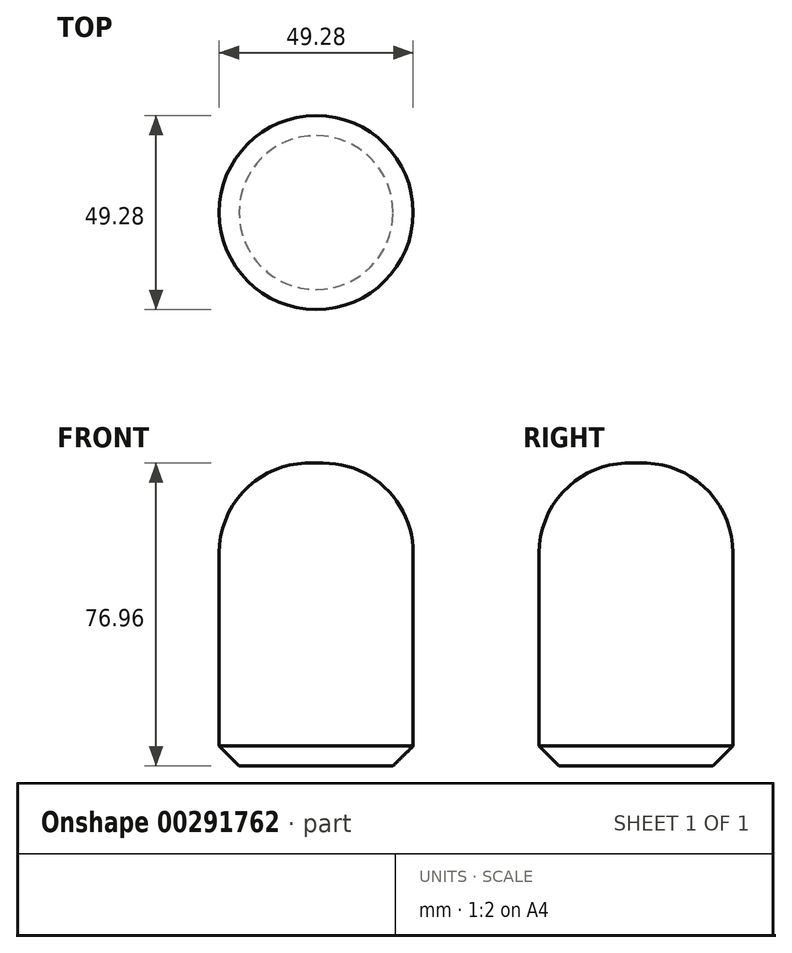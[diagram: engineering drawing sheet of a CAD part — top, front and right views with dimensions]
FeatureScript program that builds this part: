
annotation { "Feature Type Name" : "Feature", "Feature Type Description" : "" }
export const myFeature = defineFeature(function(context is Context, id is Id, definition is map)
    precondition{}
    {
        {
            var Q0;
            Q0=qCreatedBy(makeId("Top.planeOp"),FACE);
            var sketch = newSketch(context, id + "F0", { "sketchPlane" : qUnion([Q0])});
            skCircle(sketch, "E0", {"center": v(0, 0) * mm, "radius": 24.64 * mm});
            skSolve(sketch);
        }
        {
            var Q0;
            Q0=makeQuery(id+"F0.imprint","IMPRINT",FACE,{"disambiguationData":[TD([[makeQuery(id+"F0.imprint","IMPRINT",EDGE,{"derivedFrom":sQuery(id+"F0.wireOp",EDGE,"E0")}),1.0]])]});
            extrude(context, id + "F1", {"entities" : qUnion([Q0]), "depth" : 51.56 * mm});
        }
        {
            var Q0;
            Q0=makeQuery(id+"F1.opExtrude","CAP_EDGE",EDGE,{"disambiguationData":[OSD([sQuery(id+"F0.wireOp",EDGE,"E0")])],"isStart":true});
            chamfer(context, id + "F2", {"entities" : qUnion([Q0]), "width" : 5.08 * mm, "tangentPropagation" : true});
        }
        {
            var Q0;
            Q0=makeQuery(id+"F1.opExtrude","CAP_FACE",FACE,{"disambiguationData":[OSD([sQuery(id+"F0.wireOp",EDGE,"E0")])],"isStart":false});
            extrude(context, id + "F3", {"entities" : qUnion([Q0]), "operationType" : NewBodyOperationType.ADD, "depth" : 25.4 * mm});
        }
        {
            var Q0;
            Q0=makeQuery(id+"F3.opExtrude","CAP_EDGE",EDGE,{"disambiguationData":[OSD([sQuery(id+"F0.wireOp",EDGE,"E0")])],"isStart":false});
            fillet(context, id + "F4", {"entities" : qUnion([Q0]), "radius" : 22.86 * mm, "tangentPropagation" : true, "allowEdgeOverflow" : false});
        }
    });
